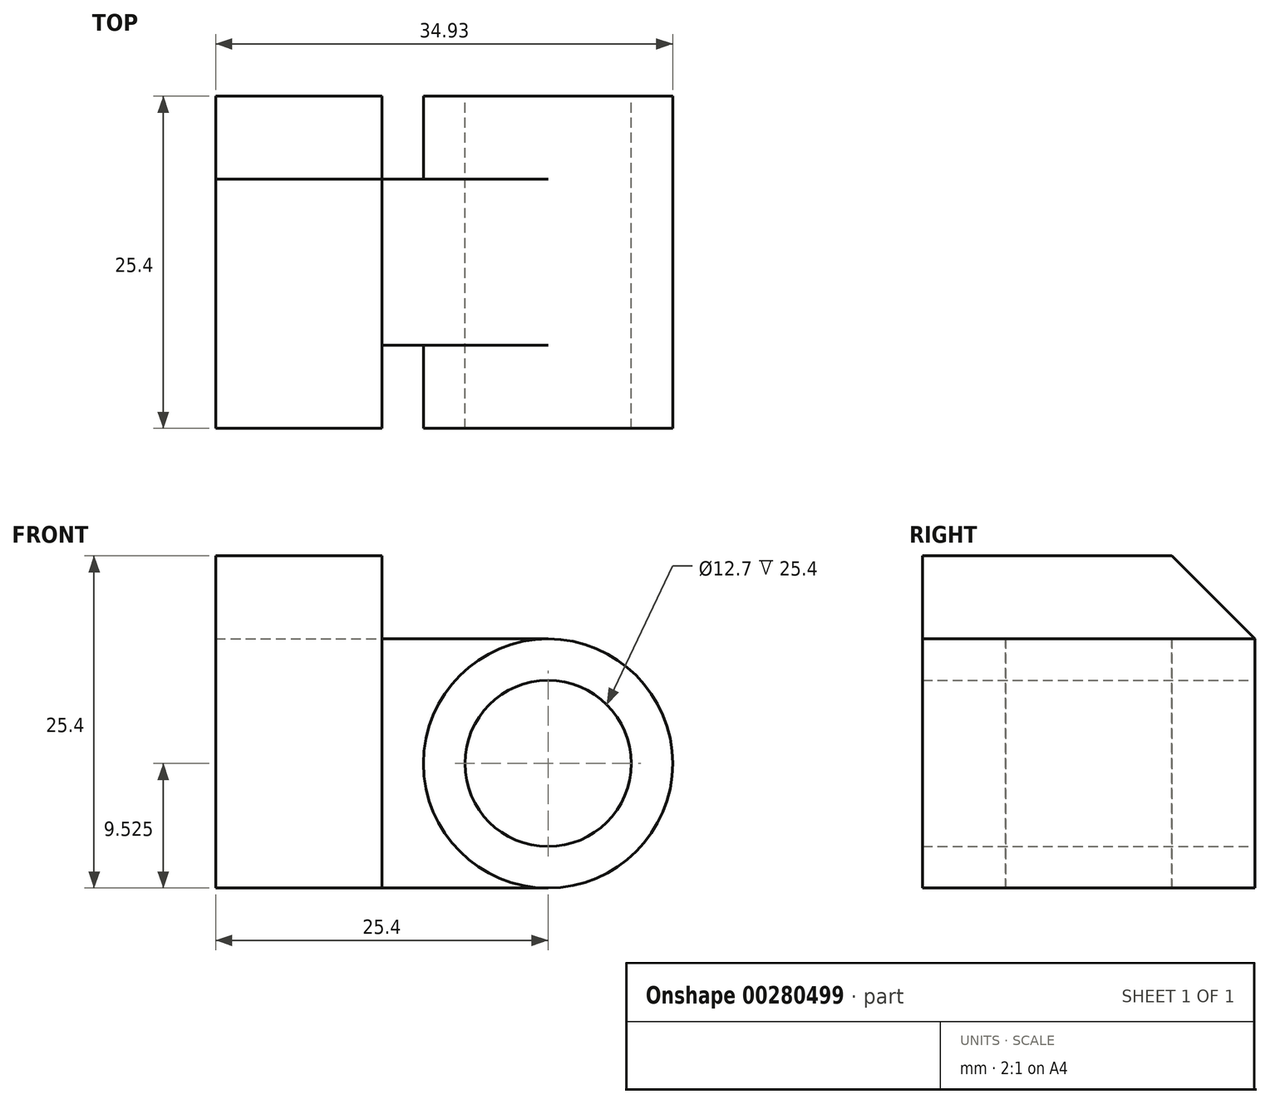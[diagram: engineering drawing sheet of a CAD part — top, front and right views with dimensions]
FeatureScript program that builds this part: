
annotation { "Feature Type Name" : "Feature", "Feature Type Description" : "" }
export const myFeature = defineFeature(function(context is Context, id is Id, definition is map)
    precondition{}
    {
        {
            var Q0;
            Q0=qCreatedBy(makeId("Front.planeOp"),FACE);
            var sketch = newSketch(context, id + "F0", { "sketchPlane" : qUnion([Q0])});
            skLineSegment(sketch, "E0", {"start": v(-12.7, 0) * mm, "end": v(0, 0) * mm});
            skLineSegment(sketch, "E1", {"start": v(0, 0) * mm, "end": v(0, 25.4) * mm});
            skLineSegment(sketch, "E2", {"start": v(0, 25.4) * mm, "end": v(-12.7, 25.4) * mm});
            skLineSegment(sketch, "E3", {"start": v(-12.7, 25.4) * mm, "end": v(-12.7, 0) * mm});
            skLineSegment(sketch, "E4", {"start": v(0, 25.4) * mm, "end": v(0, 19.05) * mm});
            skLineSegment(sketch, "E5", {"start": v(0, 19.05) * mm, "end": v(12.7, 19.05) * mm});
            skCircle(sketch, "E6", {"center": v(12.7, 9.53) * mm, "radius": 9.53 * mm});
            skPoint(sketch, "E6.first.point", {"position": v(12.7, 0) * mm});
            skPoint(sketch, "E6.third.point", {"position": v(12.7, 0) * mm});
            skCircle(sketch, "E7", {"center": v(12.7, 9.53) * mm, "radius": 6.35 * mm});
            skLineSegment(sketch, "E8", {"start": v(0, 0) * mm, "end": v(12.7, 0) * mm});
            skSolve(sketch);
        }
        {
            var Q0;
            Q0=makeQuery(id+"F0.imprint","IMPRINT",FACE,{"disambiguationData":[TD([[makeQuery(id+"F0.imprint","IMPRINT",EDGE,{"derivedFrom":sQuery(id+"F0.wireOp",EDGE,"E0")}),1.0]])]});
            var Q1;
            Q1=makeQuery(id+"F0.imprint","IMPRINT",FACE,{"disambiguationData":[TD([[makeQuery(id+"F0.imprint","IMPRINT",EDGE,{"derivedFrom":sQuery(id+"F0.wireOp",EDGE,"E7")}),-1.0]])]});
            extrude(context, id + "F1", {"entities" : qUnion([Q0, Q1]), "endBound" : BoundingType.SYMMETRIC, "depth" : 25.4 * mm});
        }
        {
            var Q0;
            Q0=makeQuery(id+"F0.imprint","IMPRINT",FACE,{"disambiguationData":[TD([[makeQuery(id+"F0.imprint","IMPRINT",EDGE,{"derivedFrom":sQuery(id+"F0.wireOp",EDGE,"E1")}),-1.0]])]});
            extrude(context, id + "F2", {"entities" : qUnion([Q0]), "operationType" : NewBodyOperationType.ADD, "endBound" : BoundingType.SYMMETRIC, "depth" : 12.7 * mm});
        }
        {
            var Q0;
            Q0=makeQuery(id+"F1.opExtrude","SWEPT_FACE",FACE,{"disambiguationData":[OSD([sQuery(id+"F0.wireOp",EDGE,"E1"),sQuery(id+"F0.wireOp",EDGE,"E4")])]});
            var sketch = newSketch(context, id + "F3", { "sketchPlane" : qUnion([Q0])});
            skLineSegment(sketch, "E9", {"start": v(-6.35, 25.4) * mm, "end": v(6.35, 25.4) * mm});
            skLineSegment(sketch, "E10", {"start": v(6.35, 25.4) * mm, "end": v(12.7, 19.05) * mm});
            skLineSegment(sketch, "E11", {"start": v(12.7, 19.05) * mm, "end": v(12.7, 25.4) * mm});
            skLineSegment(sketch, "E12", {"start": v(-12.7, 25.4) * mm, "end": v(-12.7, 19.05) * mm});
            skLineSegment(sketch, "E13", {"start": v(-12.7, 19.05) * mm, "end": v(-6.35, 25.4) * mm});
            skSolve(sketch);
        }
        {
            var Q0;
            {var subQ0=sQuery(id+"F3.wireOp",EDGE,"E12");Q0=makeQuery(id+"F3.imprint","IMPRINT",FACE,{"disambiguationData":[TD([[makeQuery(id+"F3.imprint","IMPRINT",EDGE,{"derivedFrom":subQ0}),1.0]])]});}
            var Q1;
            {var subQ0=sQuery(id+"F3.wireOp",EDGE,"E10");Q1=makeQuery(id+"F3.imprint","IMPRINT",FACE,{"disambiguationData":[TD([[makeQuery(id+"F3.imprint","IMPRINT",EDGE,{"derivedFrom":subQ0}),1.0]])]});}
            extrude(context, id + "F4", {"entities" : qUnion([Q0, Q1]), "operationType" : NewBodyOperationType.REMOVE, "endBound" : BoundingType.THROUGH_ALL, "oppositeDirection" : true, "depth" : 25.4 * mm});
        }
    });
